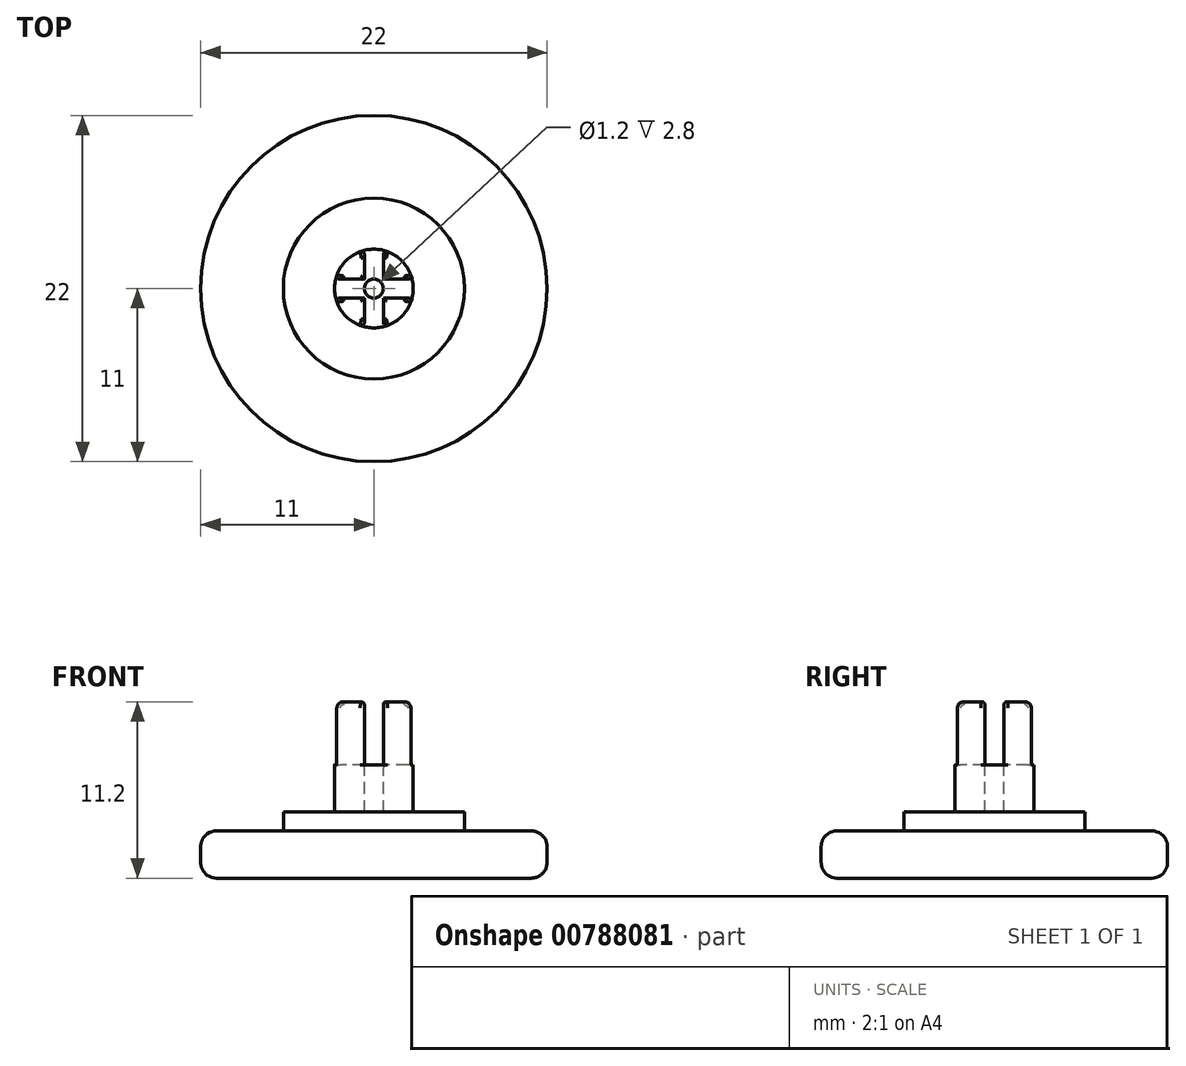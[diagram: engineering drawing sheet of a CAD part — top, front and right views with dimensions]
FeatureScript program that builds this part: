
annotation { "Feature Type Name" : "Feature", "Feature Type Description" : "" }
export const myFeature = defineFeature(function(context is Context, id is Id, definition is map)
    precondition{}
    {
        {
            var Q0;
            Q0=qCreatedBy(makeId("Top.planeOp"),FACE);
            var sketch = newSketch(context, id + "F0", { "sketchPlane" : qUnion([Q0])});
            skCircle(sketch, "E0", {"center": v(0, 0) * mm, "radius": 11 * mm});
            skSolve(sketch);
        }
        {
            var Q0;
            Q0=qSketchRegion(id+"F0",true);
            extrude(context, id + "F1", {"entities" : qUnion([Q0]), "depth" : 3 * mm});
        }
        {
            var Q0;
            Q0=makeQuery(id+"F1.opExtrude","CAP_FACE",FACE,{"disambiguationData":[OSD([sQuery(id+"F0.wireOp",EDGE,"E0")])],"isStart":false});
            var sketch = newSketch(context, id + "F2", { "sketchPlane" : qUnion([Q0])});
            skCircle(sketch, "E1", {"center": v(0, 0) * mm, "radius": 5.75 * mm});
            skSolve(sketch);
        }
        {
            var Q0;
            Q0=qSketchRegion(id+"F2",true);
            extrude(context, id + "F3", {"entities" : qUnion([Q0]), "operationType" : NewBodyOperationType.ADD, "depth" : 1.2 * mm});
        }
        {
            var Q0;
            Q0=makeQuery(id+"F3.opExtrude","CAP_FACE",FACE,{"disambiguationData":[OSD([sQuery(id+"F2.wireOp",EDGE,"E1")])],"isStart":false});
            var sketch = newSketch(context, id + "F4", { "sketchPlane" : qUnion([Q0])});
            skCircle(sketch, "E2", {"center": v(0, 0) * mm, "radius": 2.5 * mm});
            skSolve(sketch);
        }
        {
            var Q0;
            Q0=qSketchRegion(id+"F4",true);
            extrude(context, id + "F5", {"entities" : qUnion([Q0]), "operationType" : NewBodyOperationType.ADD, "depth" : 7 * mm});
        }
        {
            var Q0;
            Q0=makeQuery(id+"F5.opExtrude","CAP_FACE",FACE,{"disambiguationData":[OSD([sQuery(id+"F4.wireOp",EDGE,"E2")])],"isStart":false});
            var sketch = newSketch(context, id + "F6", { "sketchPlane" : qUnion([Q0])});
            skCircle(sketch, "E3", {"center": v(0, 0) * mm, "radius": 0.6 * mm});
            skSolve(sketch);
        }
        {
            var Q0;
            Q0=makeQuery(id+"F3.opExtrude","CAP_FACE",FACE,{"disambiguationData":[OSD([sQuery(id+"F2.wireOp",EDGE,"E1")])],"isStart":false});
            cPlane(context, id + "F7", {"entities" : qUnion([Q0]), "cplaneType" : CPlaneType.OFFSET, "offset" : 6 * mm, "width" : 152.4 * mm, "height" : 152.4 * mm});
        }
        {
            var Q0;
            Q0=qCreatedBy(id+"F7.planeOp",FACE);
            var sketch = newSketch(context, id + "F8", { "sketchPlane" : qUnion([Q0])});
            skCircle(sketch, "E4", {"center": v(0, 0) * mm, "radius": 2 * mm});
            skCircle(sketch, "E5", {"center": v(0, 0) * mm, "radius": 2.2 * mm});
            skSolve(sketch);
        }
        {
            var Q0;
            Q0=makeQuery(id+"F8.imprint","IMPRINT",FACE,{"disambiguationData":[TD([[makeQuery(id+"F8.imprint","IMPRINT",EDGE,{"derivedFrom":sQuery(id+"F8.wireOp",EDGE,"E4")}),-1.0]])]});
            extrude(context, id + "F9", {"entities" : qUnion([Q0]), "operationType" : NewBodyOperationType.ADD, "depth" : 0.4 * mm});
        }
        {
            var Q0;
            Q0=qSketchRegion(id+"F6",true);
            extrude(context, id + "F10", {"entities" : qUnion([Q0]), "operationType" : NewBodyOperationType.REMOVE, "oppositeDirection" : true, "depth" : 7 * mm});
        }
        {
            var Q0;
            Q0=makeQuery(id+"F5.opExtrude","CAP_FACE",FACE,{"disambiguationData":[OSD([sQuery(id+"F4.wireOp",EDGE,"E2")])],"isStart":false});
            var sketch = newSketch(context, id + "F11", { "sketchPlane" : qUnion([Q0])});
            skLineSegment(sketch, "E6.bottom", {"start": v(-0.6, 3.43) * mm, "end": v(0.6, 3.43) * mm});
            skLineSegment(sketch, "E6.top", {"start": v(-0.6, -3.43) * mm, "end": v(0.6, -3.43) * mm});
            skLineSegment(sketch, "E6.left", {"start": v(-0.6, 3.43) * mm, "end": v(-0.6, -3.43) * mm});
            skLineSegment(sketch, "E6.right", {"start": v(0.6, 3.43) * mm, "end": v(0.6, -3.43) * mm});
            skPoint(sketch, "E6.middle", {"position": v(0, 0) * mm});
            skLineSegment(sketch, "E7.bottom", {"start": v(3.6, 0.6) * mm, "end": v(-3.6, 0.6) * mm});
            skLineSegment(sketch, "E7.top", {"start": v(3.6, -0.6) * mm, "end": v(-3.6, -0.6) * mm});
            skLineSegment(sketch, "E7.left", {"start": v(3.6, 0.6) * mm, "end": v(3.6, -0.6) * mm});
            skLineSegment(sketch, "E7.right", {"start": v(-3.6, 0.6) * mm, "end": v(-3.6, -0.6) * mm});
            skSolve(sketch);
        }
        {
            var Q0;
            Q0=qSketchRegion(id+"F11",true);
            extrude(context, id + "F12", {"entities" : qUnion([Q0]), "operationType" : NewBodyOperationType.REMOVE, "oppositeDirection" : true, "depth" : 4 * mm});
        }
        {
            var Q0;
            {var subQ0=sQuery(id+"F4.wireOp",EDGE,"E2");Q0=makeQuery(id+"F12.boolean.opBoolean","SPLIT",EDGE,{"disambiguationData":[TD([makeQuery(id+"F12.opExtrude","SWEPT_FACE",FACE,{"disambiguationData":[OSD([sQuery(id+"F11.wireOp",EDGE,"E6.left")])]})])],"derivedFrom":makeQuery(id+"F5.opExtrude","CAP_EDGE",EDGE,{"disambiguationData":[OSD([subQ0])],"isStart":false})});}
            var Q1;
            {var subQ0=sQuery(id+"F4.wireOp",EDGE,"E2");Q1=makeQuery(id+"F12.boolean.opBoolean","SPLIT",EDGE,{"disambiguationData":[TD([makeQuery(id+"F12.opExtrude","SWEPT_FACE",FACE,{"disambiguationData":[OSD([sQuery(id+"F11.wireOp",EDGE,"E6.right")])]})])],"derivedFrom":makeQuery(id+"F5.opExtrude","CAP_EDGE",EDGE,{"disambiguationData":[OSD([subQ0])],"isStart":false})});}
            fillet(context, id + "F13", {"entities" : qUnion([Q0, Q1]), "radius" : .4 * mm, "tangentPropagation" : true, "allowEdgeOverflow" : false});
        }
        {
            var Q0;
            Q0=makeQuery(id+"F1.opExtrude","CAP_EDGE",EDGE,{"disambiguationData":[OSD([sQuery(id+"F0.wireOp",EDGE,"E0")])],"isStart":false});
            var Q1;
            Q1=makeQuery(id+"F1.opExtrude","CAP_EDGE",EDGE,{"disambiguationData":[OSD([sQuery(id+"F0.wireOp",EDGE,"E0")])],"isStart":true});
            fillet(context, id + "F14", {"entities" : qUnion([Q0, Q1]), "radius" : 1 * mm, "tangentPropagation" : true, "allowEdgeOverflow" : false});
        }
        {
            var Q0;
            {var subQ0=sQuery(id+"F4.wireOp",EDGE,"E2");var subQ1=sQuery(id+"F11.wireOp",EDGE,"E7.bottom");var subQ2=sQuery(id+"F11.wireOp",EDGE,"E6.left");var subQ3=makeQuery(id+"F11.imprint","INTERSECT",VERTEX,{"derivedFrom":[subQ2,subQ1]});Q0=makeQuery(id+"F12.boolean.opBoolean","SPLIT",FACE,{"disambiguationData":[TD([makeQuery(id+"F12.opExtrude","SWEPT_FACE",FACE,{"disambiguationData":[OSD([subQ2]),TDD([makeQuery(id+"F11.imprint","IMPRINT",EDGE,{"disambiguationData":[TD([[makeQuery(id+"F11.imprint","INTERSECT",VERTEX,{"derivedFrom":[sQuery(id+"F11.wireOp",EDGE,"E6.bottom"),subQ2]}),-1.0]])],"derivedFrom":subQ2}),makeQuery(id+"F11.imprint","IMPRINT",EDGE,{"disambiguationData":[TD([[subQ3,1.0]])],"derivedFrom":subQ2})])]})])],"derivedFrom":makeQuery(id+"F5.opExtrude","CAP_FACE",FACE,{"disambiguationData":[OSD([subQ0])],"isStart":false})});}
            var Q1;
            {var subQ0=sQuery(id+"F4.wireOp",EDGE,"E2");var subQ1=sQuery(id+"F11.wireOp",EDGE,"E7.bottom");var subQ2=sQuery(id+"F11.wireOp",EDGE,"E6.right");var subQ3=makeQuery(id+"F11.imprint","INTERSECT",VERTEX,{"derivedFrom":[subQ2,subQ1]});Q1=makeQuery(id+"F12.boolean.opBoolean","SPLIT",FACE,{"disambiguationData":[TD([makeQuery(id+"F12.opExtrude","SWEPT_FACE",FACE,{"disambiguationData":[OSD([subQ2]),TDD([makeQuery(id+"F11.imprint","IMPRINT",EDGE,{"disambiguationData":[TD([[makeQuery(id+"F11.imprint","INTERSECT",VERTEX,{"derivedFrom":[sQuery(id+"F11.wireOp",EDGE,"E6.bottom"),subQ2]}),-1.0]])],"derivedFrom":subQ2}),makeQuery(id+"F11.imprint","IMPRINT",EDGE,{"disambiguationData":[TD([[subQ3,1.0]])],"derivedFrom":subQ2})])]})])],"derivedFrom":makeQuery(id+"F5.opExtrude","CAP_FACE",FACE,{"disambiguationData":[OSD([subQ0])],"isStart":false})});}
            var Q2;
            {var subQ0=sQuery(id+"F4.wireOp",EDGE,"E2");var subQ1=sQuery(id+"F11.wireOp",EDGE,"E7.top");var subQ2=sQuery(id+"F11.wireOp",EDGE,"E6.right");var subQ3=makeQuery(id+"F11.imprint","INTERSECT",VERTEX,{"derivedFrom":[subQ2,subQ1]});Q2=makeQuery(id+"F12.boolean.opBoolean","SPLIT",FACE,{"disambiguationData":[TD([makeQuery(id+"F12.opExtrude","SWEPT_FACE",FACE,{"disambiguationData":[OSD([subQ2]),TDD([makeQuery(id+"F11.imprint","IMPRINT",EDGE,{"disambiguationData":[TD([[subQ3,-1.0]])],"derivedFrom":subQ2}),makeQuery(id+"F11.imprint","IMPRINT",EDGE,{"disambiguationData":[TD([[makeQuery(id+"F11.imprint","INTERSECT",VERTEX,{"derivedFrom":[sQuery(id+"F11.wireOp",EDGE,"E6.top"),subQ2]}),1.0]])],"derivedFrom":subQ2})])]})])],"derivedFrom":makeQuery(id+"F5.opExtrude","CAP_FACE",FACE,{"disambiguationData":[OSD([subQ0])],"isStart":false})});}
            var Q3;
            {var subQ0=sQuery(id+"F4.wireOp",EDGE,"E2");var subQ1=sQuery(id+"F11.wireOp",EDGE,"E6.left");var subQ4=sQuery(id+"F11.wireOp",EDGE,"E7.top");var subQ5=makeQuery(id+"F11.imprint","INTERSECT",VERTEX,{"derivedFrom":[subQ1,subQ4]});Q3=makeQuery(id+"F12.boolean.opBoolean","SPLIT",FACE,{"disambiguationData":[TD([makeQuery(id+"F12.opExtrude","SWEPT_FACE",FACE,{"disambiguationData":[OSD([subQ1]),TDD([makeQuery(id+"F11.imprint","IMPRINT",EDGE,{"disambiguationData":[TD([[subQ5,-1.0]])],"derivedFrom":subQ1}),makeQuery(id+"F11.imprint","IMPRINT",EDGE,{"disambiguationData":[TD([[makeQuery(id+"F11.imprint","INTERSECT",VERTEX,{"derivedFrom":[sQuery(id+"F11.wireOp",EDGE,"E6.top"),subQ1]}),1.0]])],"derivedFrom":subQ1})])]})])],"derivedFrom":makeQuery(id+"F5.opExtrude","CAP_FACE",FACE,{"disambiguationData":[OSD([subQ0])],"isStart":false})});}
            var Q4;
            Q4=makeQuery(id+"F12.boolean.opBoolean","INTERSECT",EDGE,{"derivedFrom":[makeQuery(id+"F10.boolean.opBoolean","COPY",FACE,{"derivedFrom":makeQuery(id+"F10.opExtrude","SWEPT_FACE",FACE,{"disambiguationData":[OSD([sQuery(id+"F6.wireOp",EDGE,"E3")])]})}),makeQuery(id+"F12.opExtrude","CAP_FACE",FACE,{"disambiguationData":[OSD([sQuery(id+"F11.wireOp",EDGE,"E6.bottom"),sQuery(id+"F11.wireOp",EDGE,"E6.top"),sQuery(id+"F11.wireOp",EDGE,"E6.left"),sQuery(id+"F11.wireOp",EDGE,"E6.right"),sQuery(id+"F11.wireOp",EDGE,"E7.bottom"),sQuery(id+"F11.wireOp",EDGE,"E7.top"),sQuery(id+"F11.wireOp",EDGE,"E7.left"),sQuery(id+"F11.wireOp",EDGE,"E7.right")])],"isStart":false})]});
            fillet(context, id + "F15", {"entities" : qUnion([Q0, Q1, Q2, Q3, Q4]), "radius" : 0.2 * mm, "tangentPropagation" : true, "allowEdgeOverflow" : false});
        }
    });
